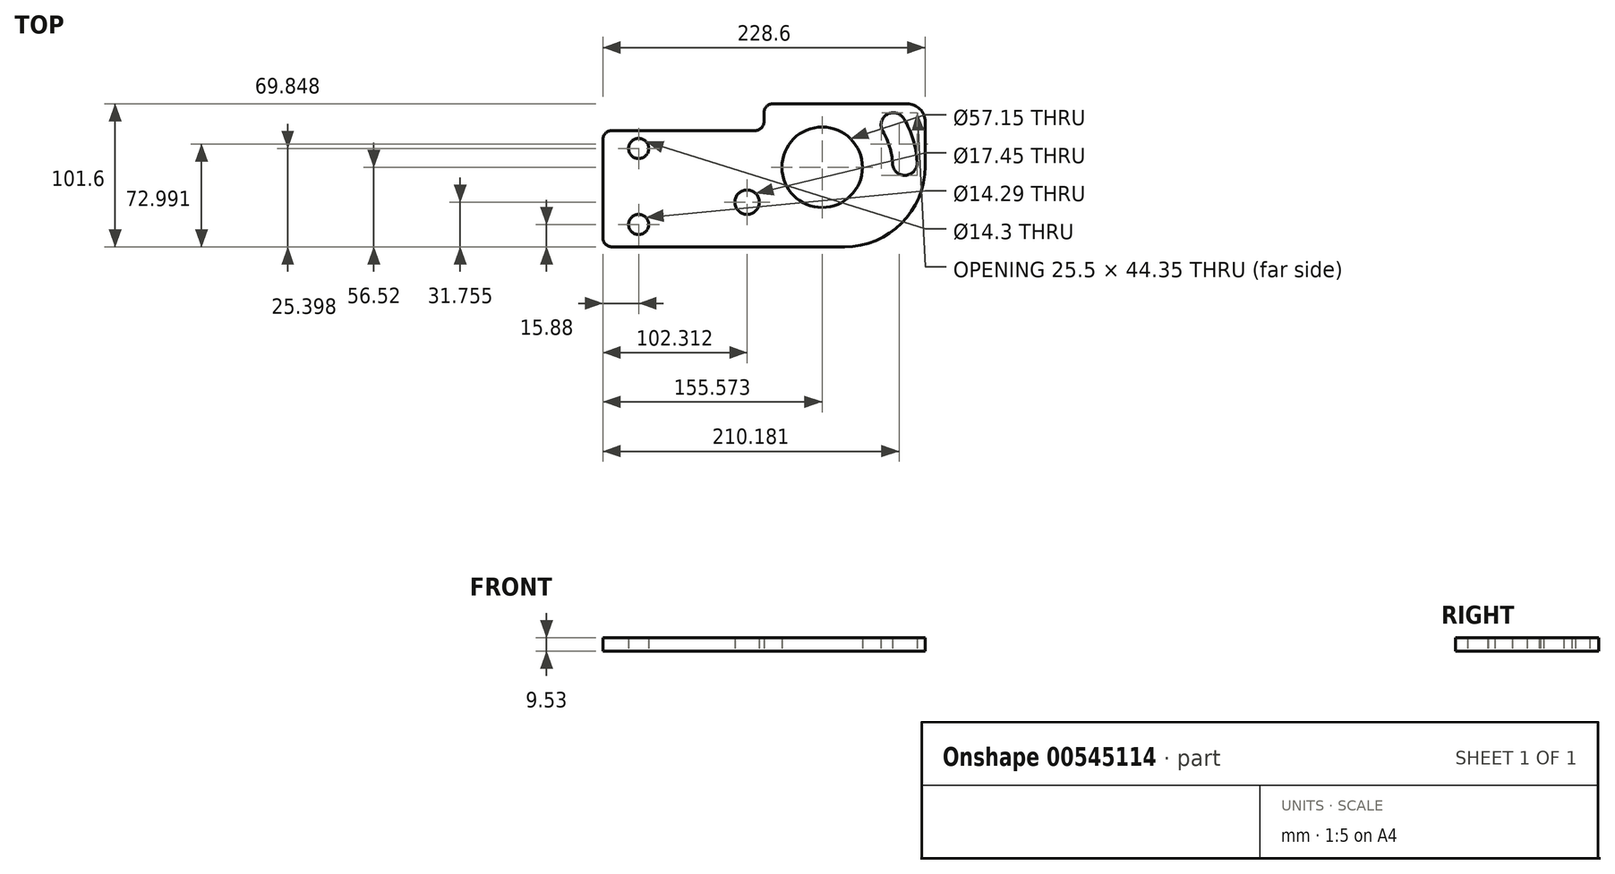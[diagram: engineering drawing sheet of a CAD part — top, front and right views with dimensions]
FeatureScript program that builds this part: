
annotation { "Feature Type Name" : "Feature", "Feature Type Description" : "" }
export const myFeature = defineFeature(function(context is Context, id is Id, definition is map)
    precondition{}
    {
        {
            var Q0;
            Q0=qCreatedBy(makeId("Top.planeOp"),FACE);
            var sketch = newSketch(context, id + "F0", { "sketchPlane" : qUnion([Q0])});
            skLineSegment(sketch, "E0.bottom", {"start": v(-2.57, 53.96) * mm, "end": v(92.68, 53.96) * mm});
            skLineSegment(sketch, "E0.top", {"start": v(-116.87, -47.64) * mm, "end": v(48.23, -47.64) * mm});
            skLineSegment(sketch, "E0.left", {"start": v(-123.22, 28.56) * mm, "end": v(-123.22, -41.29) * mm});
            skLineSegment(sketch, "E0.right", {"start": v(105.38, 41.26) * mm, "end": v(105.38, 9.51) * mm});
            skCircle(sketch, "E1", {"center": v(32.35, 8.88) * mm, "radius": 28.58 * mm});
            skArc(sketch, "E2", {"start": v(90.35, 43.35) * mm, "mid": v(78.39, 46.39) * mm, "end": v(75.35, 34.43) * mm});
            skArc(sketch, "E3", {"start": v(82.29, 11.68) * mm, "mid": v(91.48, 3.18) * mm, "end": v(99.71, 12.62) * mm});
            skCircle(sketch, "E4", {"center": v(-20.9, -15.89) * mm, "radius": 8.72 * mm});
            skCircle(sketch, "E5", {"center": v(-97.82, -31.76) * mm, "radius": 7.14 * mm});
            skCircle(sketch, "E6", {"center": v(-97.82, 22.2) * mm, "radius": 7.15 * mm});
            skArc(sketch, "E7.trimOffspring", {"start": v(82.31, 11.2) * mm, "mid": v(80.26, 23.25) * mm, "end": v(75.35, 34.43) * mm});
            skPoint(sketch, "E8.orphan", {"position": v(-43, -15.89) * mm});
            skArc(sketch, "E9.trimOffspring", {"start": v(99.74, 12.06) * mm, "mid": v(96.97, 28.28) * mm, "end": v(90.35, 43.35) * mm});
            skPoint(sketch, "E10.visualSharp", {"position": v(105.38, 53.96) * mm});
            skArc(sketch, "E10.filletArc", {"start": v(105.38, 41.26) * mm, "mid": v(101.66, 50.24) * mm, "end": v(92.68, 53.96) * mm});
            skPoint(sketch, "E11.visualSharp", {"position": v(105.38, -47.64) * mm});
            skArc(sketch, "E11.filletArc", {"start": v(48.23, -47.64) * mm, "mid": v(88.64, -30.9) * mm, "end": v(105.38, 9.51) * mm});
            skLineSegment(sketch, "E12", {"start": v(-116.87, 34.91) * mm, "end": v(-15.27, 34.91) * mm});
            skLineSegment(sketch, "E13", {"start": v(-8.92, 41.26) * mm, "end": v(-8.92, 47.61) * mm});
            skPoint(sketch, "E14.orphan", {"position": v(-123.22, 53.96) * mm});
            skPoint(sketch, "E15.visualSharp", {"position": v(-8.92, 34.91) * mm});
            skArc(sketch, "E15.filletArc", {"start": v(-15.27, 34.91) * mm, "mid": v(-10.78, 36.77) * mm, "end": v(-8.92, 41.26) * mm});
            skPoint(sketch, "E16.visualSharp", {"position": v(-8.92, 53.96) * mm});
            skArc(sketch, "E16.filletArc", {"start": v(-2.57, 53.96) * mm, "mid": v(-7.06, 52.1) * mm, "end": v(-8.92, 47.61) * mm});
            skPoint(sketch, "E17.visualSharp", {"position": v(-123.22, 34.91) * mm});
            skArc(sketch, "E17.filletArc", {"start": v(-116.87, 34.91) * mm, "mid": v(-121.36, 33.05) * mm, "end": v(-123.22, 28.56) * mm});
            skPoint(sketch, "E18.visualSharp", {"position": v(-123.22, -47.64) * mm});
            skArc(sketch, "E18.filletArc", {"start": v(-123.22, -41.29) * mm, "mid": v(-121.36, -45.78) * mm, "end": v(-116.87, -47.64) * mm});
            skSolve(sketch);
        }
        {
            var Q0;
            Q0=makeQuery(id+"F0.imprint","IMPRINT",FACE,{"disambiguationData":[TD([[makeQuery(id+"F0.imprint","IMPRINT",EDGE,{"derivedFrom":sQuery(id+"F0.wireOp",EDGE,"E0.bottom")}),-1.0]])]});
            extrude(context, id + "F1", {"entities" : qUnion([Q0]), "depth" : 9.52 * mm, "offsetDistance" : 25.4 * mm});
        }
    });
